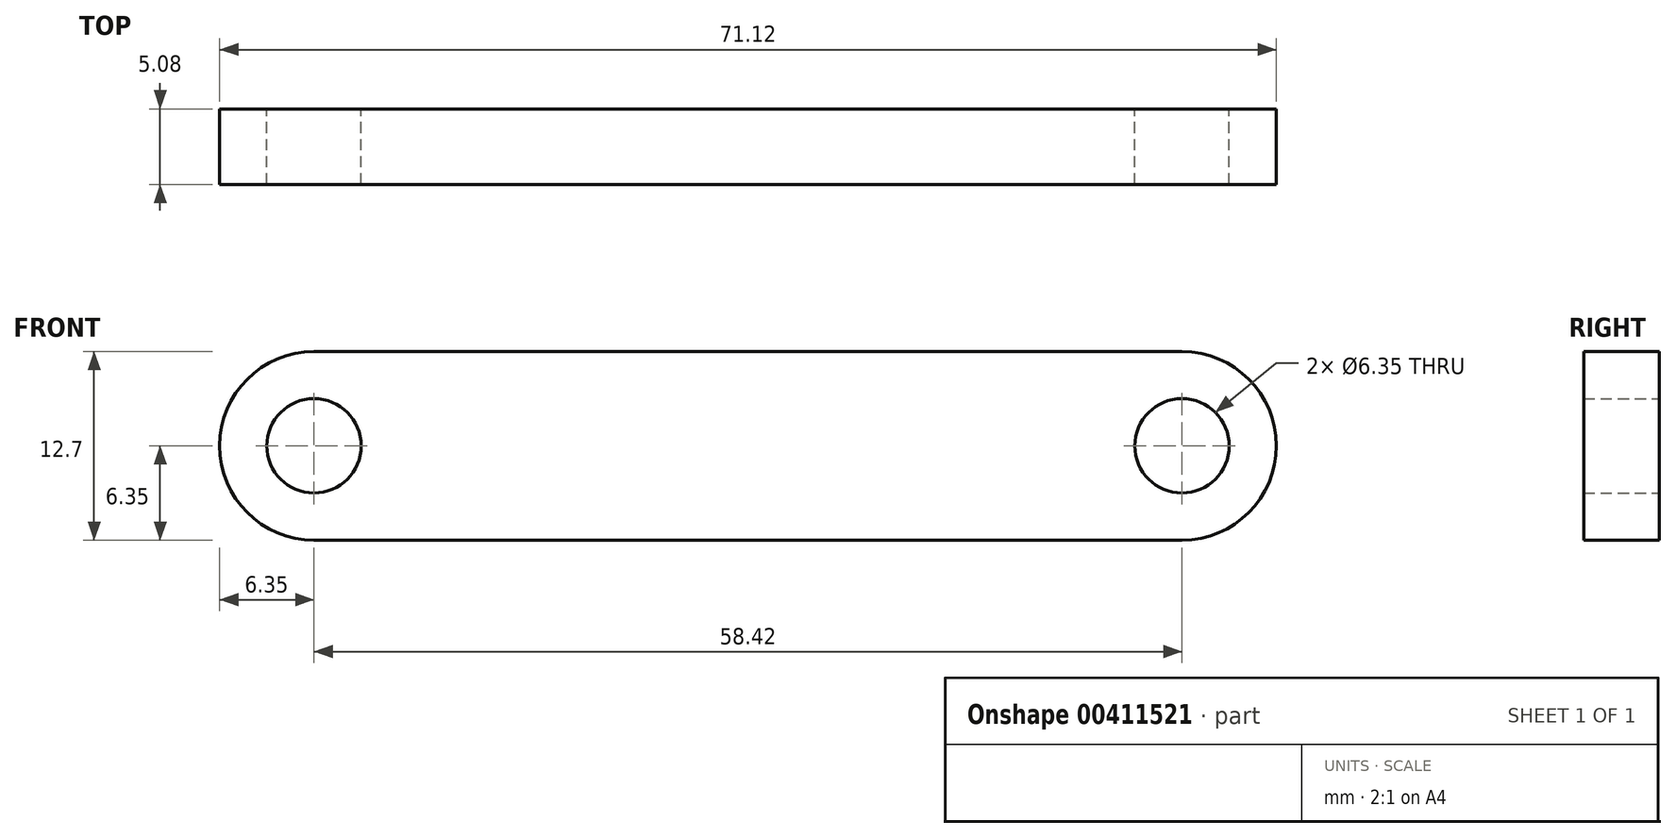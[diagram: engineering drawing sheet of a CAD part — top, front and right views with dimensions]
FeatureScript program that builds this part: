
annotation { "Feature Type Name" : "Feature", "Feature Type Description" : "" }
export const myFeature = defineFeature(function(context is Context, id is Id, definition is map)
    precondition{}
    {
        {
            var Q0;
            Q0=qCreatedBy(makeId("Front.planeOp"),FACE);
            var sketch = newSketch(context, id + "F0", { "sketchPlane" : qUnion([Q0])});
            skArc(sketch, "E0", {"start": v(0, 6.35) * mm, "mid": v(-6.35, 0) * mm, "end": v(0, -6.35) * mm});
            skArc(sketch, "E1", {"start": v(58.42, -6.35) * mm, "mid": v(64.77, 0) * mm, "end": v(58.42, 6.35) * mm});
            skLineSegment(sketch, "E2", {"start": v(0, 6.35) * mm, "end": v(58.42, 6.35) * mm});
            skLineSegment(sketch, "E3", {"start": v(0, -6.35) * mm, "end": v(58.42, -6.35) * mm});
            skCircle(sketch, "E4", {"center": v(58.42, 0) * mm, "radius": 3.18 * mm});
            skCircle(sketch, "E5", {"center": v(0, 0) * mm, "radius": 3.18 * mm});
            skSolve(sketch);
        }
        {
            var Q0;
            Q0=makeQuery(id+"F0.imprint","IMPRINT",FACE,{"disambiguationData":[TD([[makeQuery(id+"F0.imprint","IMPRINT",EDGE,{"derivedFrom":sQuery(id+"F0.wireOp",EDGE,"E0")}),1.0]])]});
            extrude(context, id + "F1", {"entities" : qUnion([Q0]), "offsetDistance" : 25.4 * mm, "depth" : 5.08 * mm});
        }
    });
